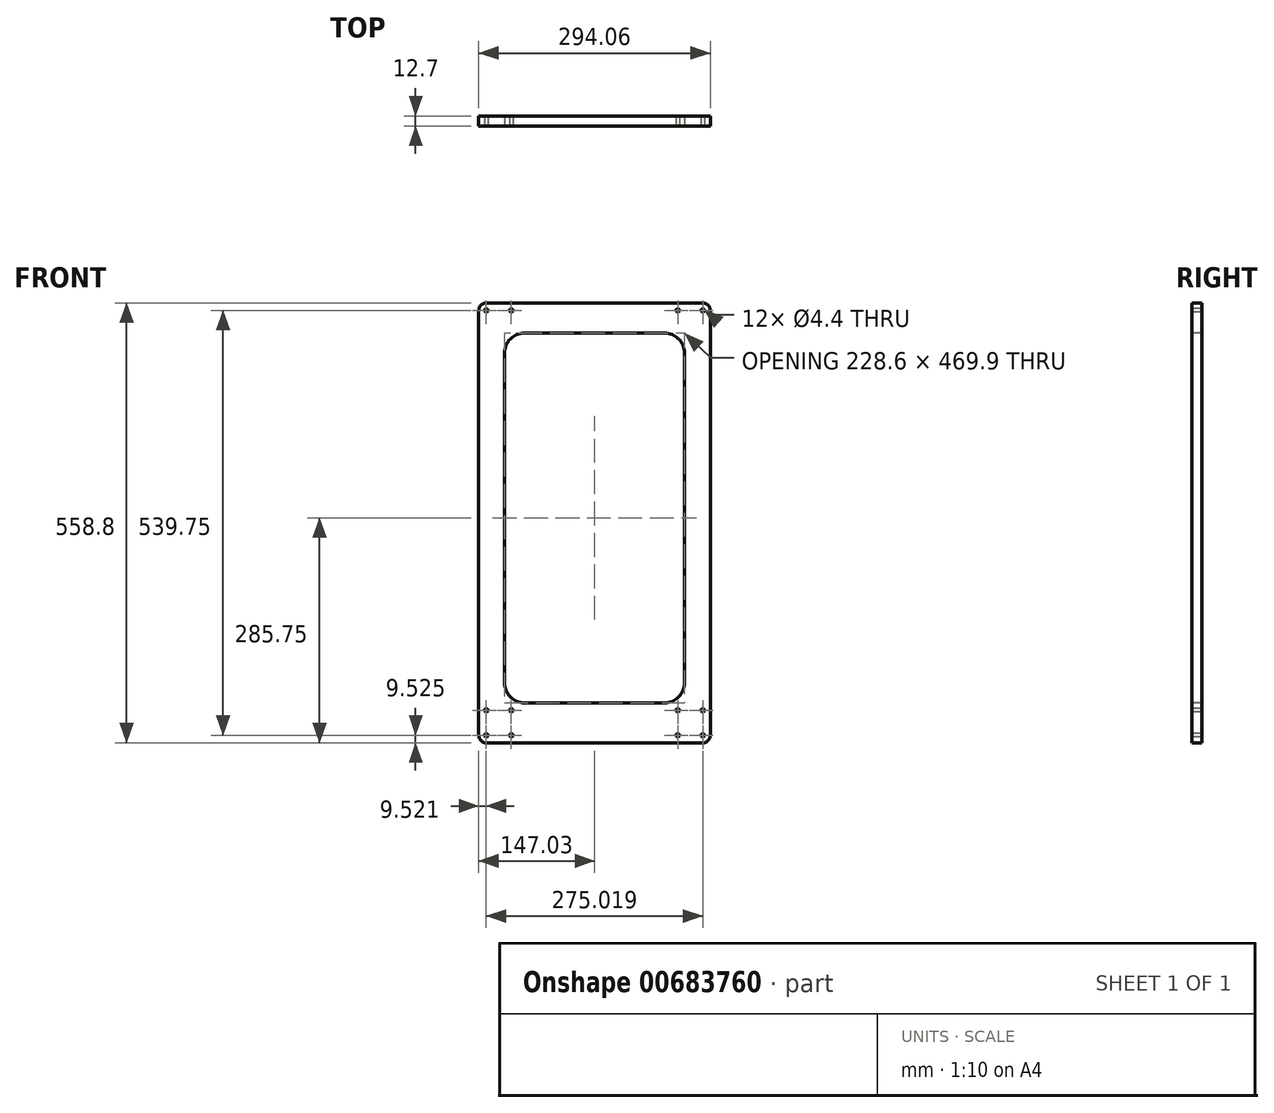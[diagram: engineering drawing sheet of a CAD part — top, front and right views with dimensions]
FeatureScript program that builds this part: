
annotation { "Feature Type Name" : "Feature", "Feature Type Description" : "" }
export const myFeature = defineFeature(function(context is Context, id is Id, definition is map)
    precondition{}
    {
        {
            var Q0;
            Q0=qCreatedBy(makeId("Front.planeOp"),FACE);
            var sketch = newSketch(context, id + "F0", { "sketchPlane" : qUnion([Q0])});
            skLineSegment(sketch, "E0.bottom", {"start": v(147.03, 279.4) * mm, "end": v(-147.03, 279.4) * mm});
            skLineSegment(sketch, "E0.top", {"start": v(147.03, -279.4) * mm, "end": v(-147.03, -279.4) * mm});
            skLineSegment(sketch, "E0.left", {"start": v(147.03, 279.4) * mm, "end": v(147.03, -279.4) * mm});
            skLineSegment(sketch, "E0.right", {"start": v(-147.03, 279.4) * mm, "end": v(-147.03, -279.4) * mm});
            skPoint(sketch, "E0.middle", {"position": v(0, 0) * mm});
            skSolve(sketch);
        }
        {
            var Q0;
            Q0 = qSketchRegion(id + "F0", true);
            extrude(context, id + "F1", {"entities" : qUnion([Q0]), "depth" : 12.7 * mm, "offsetDistance" : 25.4 * mm});
        }
        {
            var Q0;
            Q0=makeQuery(id+"F1.opExtrude","CAP_FACE",FACE,{"disambiguationData":[OSD([sQuery(id+"F0.wireOp",EDGE,"E0.bottom"),sQuery(id+"F0.wireOp",EDGE,"E0.top"),sQuery(id+"F0.wireOp",EDGE,"E0.left"),sQuery(id+"F0.wireOp",EDGE,"E0.right")])],"isStart":false});
            var sketch = newSketch(context, id + "F2", { "sketchPlane" : qUnion([Q0])});
            skLineSegment(sketch, "E1", {"start": v(0, -279.4) * mm, "end": v(0, 0) * mm, "construction": true});
            skLineSegment(sketch, "E2", {"start": v(-147.03, -254) * mm, "end": v(147.03, -254) * mm, "construction": true});
            skLineSegment(sketch, "E3", {"start": v(-121.63, -254) * mm, "end": v(-121.63, -279.4) * mm, "construction": true});
            skPoint(sketch, "E4", {"position": v(-137.5, -238.13) * mm});
            skPoint(sketch, "E5.MirrorP", {"position": v(-137.5, -269.88) * mm});
            skPoint(sketch, "E6.MirrorP", {"position": v(-105.76, -269.88) * mm});
            skPoint(sketch, "E7.MirrorP", {"position": v(-105.76, -238.13) * mm});
            skPoint(sketch, "E8.MirrorP", {"position": v(137.5, -269.88) * mm});
            skPoint(sketch, "E9.MirrorP", {"position": v(137.5, -238.13) * mm});
            skPoint(sketch, "E10.MirrorP", {"position": v(105.76, -238.13) * mm});
            skPoint(sketch, "E11.MirrorP", {"position": v(105.76, -269.88) * mm});
            skLineSegment(sketch, "E12", {"start": v(0, 0) * mm, "end": v(147.03, 0) * mm, "construction": true});
            skPoint(sketch, "E13.MirrorP", {"position": v(137.5, 269.88) * mm});
            skPoint(sketch, "E14.MirrorP", {"position": v(105.76, 269.88) * mm});
            skPoint(sketch, "E15.MirrorP", {"position": v(-105.76, 269.88) * mm});
            skPoint(sketch, "E16.MirrorP", {"position": v(-137.5, 269.88) * mm});
            skSolve(sketch);
        }
        {
            var Q0;
            Q0=sQuery(id+"F2.wireOp",VERTEX,"E16.MirrorP");
            var Q1;
            Q1=sQuery(id+"F2.wireOp",VERTEX,"E15.MirrorP");
            var Q2;
            Q2=sQuery(id+"F2.wireOp",VERTEX,"E14.MirrorP");
            var Q3;
            Q3=sQuery(id+"F2.wireOp",VERTEX,"E13.MirrorP");
            var Q4;
            Q4=sQuery(id+"F2.wireOp",VERTEX,"E10.MirrorP");
            var Q5;
            Q5=sQuery(id+"F2.wireOp",VERTEX,"E9.MirrorP");
            var Q6;
            Q6=sQuery(id+"F2.wireOp",VERTEX,"E8.MirrorP");
            var Q7;
            Q7=sQuery(id+"F2.wireOp",VERTEX,"E11.MirrorP");
            var Q8;
            Q8=sQuery(id+"F2.wireOp",VERTEX,"E6.MirrorP");
            var Q9;
            Q9=sQuery(id+"F2.wireOp",VERTEX,"E5.MirrorP");
            var Q10;
            Q10=sQuery(id+"F2.wireOp",VERTEX,"E4");
            var Q11;
            Q11=sQuery(id+"F2.wireOp",VERTEX,"E7.MirrorP");
            var Q12;
            Q12=makeQuery(id+"F1.opExtrude","SWEPT_BODY",BODY,{"disambiguationData":[OSD([sQuery(id+"F0.wireOp",EDGE,"E0.bottom"),sQuery(id+"F0.wireOp",EDGE,"E0.top"),sQuery(id+"F0.wireOp",EDGE,"E0.left"),sQuery(id+"F0.wireOp",EDGE,"E0.right")])]});
            hole(context, id + "F3", {"style" : HoleStyle.SIMPLE, "endStyle" : HoleEndStyle.THROUGH, "standardTappedOrClearance" : lookupTablePath({ "standard" : "ISO", "fit" : "Normal", "size" : "M4", "type" : "Clearance" }), "standardBlindInLast" : lookupTablePath({ "fit" : "Standard", "standard" : "ISO", "size" : "M4", "type" : "Clearance" }), "holeDiameter" : 4.4 * mm, "majorDiameter" : 6.35 * mm, "isTappedThrough" : true, "tappedDepth" : 12.7 * mm, "tapClearance" : 3, "locations" : qUnion([Q0, Q1, Q2, Q3, Q4, Q5, Q6, Q7, Q8, Q9, Q10, Q11]), "scope" : qUnion([Q12])});
        }
        {
            var Q0;
            Q0=makeQuery(id+"F1.opExtrude","SWEPT_EDGE",EDGE,{"disambiguationData":[OSD([sQuery(id+"F0.wireOp",EDGE,"E0.bottom"),sQuery(id+"F0.wireOp",EDGE,"E0.left")])]});
            var Q1;
            Q1=makeQuery(id+"F1.opExtrude","SWEPT_EDGE",EDGE,{"disambiguationData":[OSD([sQuery(id+"F0.wireOp",EDGE,"E0.top"),sQuery(id+"F0.wireOp",EDGE,"E0.left")])]});
            var Q2;
            Q2=makeQuery(id+"F1.opExtrude","SWEPT_EDGE",EDGE,{"disambiguationData":[OSD([sQuery(id+"F0.wireOp",EDGE,"E0.top"),sQuery(id+"F0.wireOp",EDGE,"E0.right")])]});
            var Q3;
            Q3=makeQuery(id+"F1.opExtrude","SWEPT_EDGE",EDGE,{"disambiguationData":[OSD([sQuery(id+"F0.wireOp",EDGE,"E0.bottom"),sQuery(id+"F0.wireOp",EDGE,"E0.right")])]});
            fillet(context, id + "F4", {"entities" : qUnion([Q0, Q1, Q2, Q3]), "radius" : 9.52 * mm, "tangentPropagation" : true, "allowEdgeOverflow" : false});
        }
        {
            var Q0;
            Q0=makeQuery(id+"F1.opExtrude","CAP_FACE",FACE,{"disambiguationData":[OSD([sQuery(id+"F0.wireOp",EDGE,"E0.bottom"),sQuery(id+"F0.wireOp",EDGE,"E0.top"),sQuery(id+"F0.wireOp",EDGE,"E0.left"),sQuery(id+"F0.wireOp",EDGE,"E0.right")])],"isStart":false});
            var sketch = newSketch(context, id + "F5", { "sketchPlane" : qUnion([Q0])});
            skLineSegment(sketch, "E17.bottom", {"start": v(-88.9, 241.3) * mm, "end": v(88.9, 241.3) * mm});
            skLineSegment(sketch, "E17.top", {"start": v(-88.9, -228.6) * mm, "end": v(88.9, -228.6) * mm});
            skLineSegment(sketch, "E17.left", {"start": v(-114.3, 215.9) * mm, "end": v(-114.3, -203.2) * mm});
            skLineSegment(sketch, "E17.right", {"start": v(114.3, 215.9) * mm, "end": v(114.3, -203.2) * mm});
            skLineSegment(sketch, "E18", {"start": v(0, 0) * mm, "end": v(0, 241.3) * mm, "construction": true});
            skPoint(sketch, "E19.visualSharp", {"position": v(-114.3, 241.3) * mm});
            skArc(sketch, "E19.filletArc", {"start": v(-88.9, 241.3) * mm, "mid": v(-106.86, 233.86) * mm, "end": v(-114.3, 215.9) * mm});
            skPoint(sketch, "E20.visualSharp", {"position": v(114.3, 241.3) * mm});
            skArc(sketch, "E20.filletArc", {"start": v(114.3, 215.9) * mm, "mid": v(106.86, 233.86) * mm, "end": v(88.9, 241.3) * mm});
            skPoint(sketch, "E21.visualSharp", {"position": v(114.3, -228.6) * mm});
            skArc(sketch, "E21.filletArc", {"start": v(88.9, -228.6) * mm, "mid": v(106.86, -221.16) * mm, "end": v(114.3, -203.2) * mm});
            skPoint(sketch, "E22.visualSharp", {"position": v(-114.3, -228.6) * mm});
            skArc(sketch, "E22.filletArc", {"start": v(-114.3, -203.2) * mm, "mid": v(-106.86, -221.16) * mm, "end": v(-88.9, -228.6) * mm});
            skSolve(sketch);
        }
        {
            var Q0;
            Q0 = qSketchRegion(id + "F5", true);
            extrude(context, id + "F6", {"entities" : qUnion([Q0]), "operationType" : NewBodyOperationType.REMOVE, "endBound" : BoundingType.THROUGH_ALL, "oppositeDirection" : true, "depth" : 25.4 * mm, "offsetDistance" : 25.4 * mm});
        }
    });
